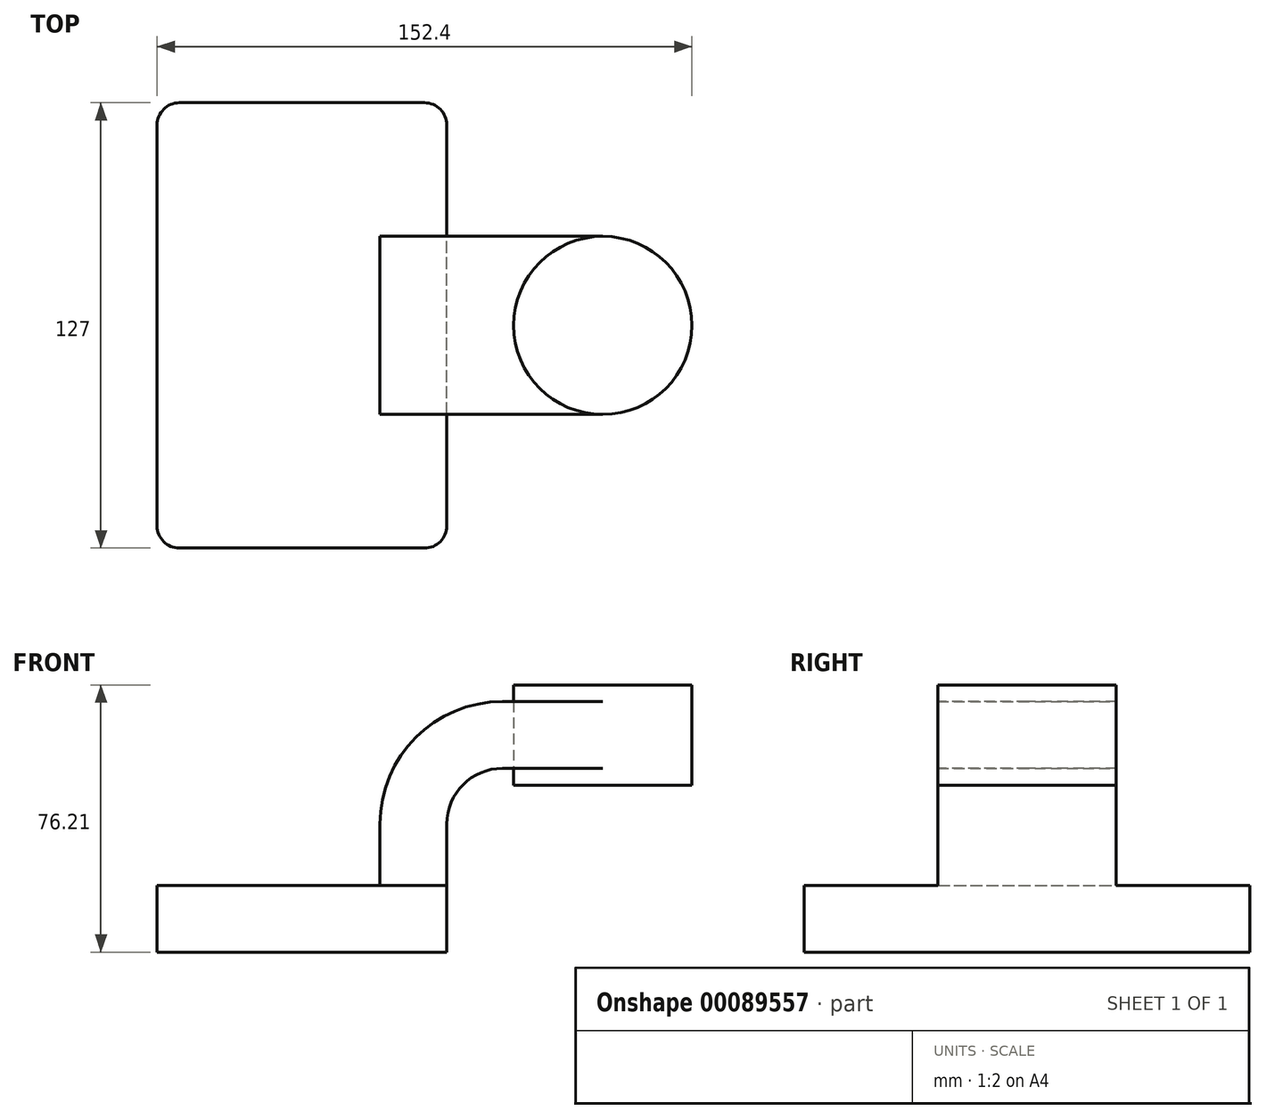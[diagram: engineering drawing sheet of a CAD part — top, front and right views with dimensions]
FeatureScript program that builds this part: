
annotation { "Feature Type Name" : "Feature", "Feature Type Description" : "" }
export const myFeature = defineFeature(function(context is Context, id is Id, definition is map)
    precondition{}
    {
        {
            var Q0;
            Q0=qCreatedBy(makeId("Front.planeOp"),FACE);
            var sketch = newSketch(context, id + "F0", { "sketchPlane" : qUnion([Q0])});
            skLineSegment(sketch, "E0.bottom", {"start": v(-41.28, -9.53) * mm, "end": v(41.28, -9.53) * mm});
            skLineSegment(sketch, "E0.top", {"start": v(-41.28, 9.52) * mm, "end": v(41.28, 9.52) * mm});
            skLineSegment(sketch, "E0.left", {"start": v(-41.28, -9.53) * mm, "end": v(-41.28, 9.53) * mm});
            skLineSegment(sketch, "E0.right", {"start": v(41.28, -9.53) * mm, "end": v(41.28, 9.53) * mm});
            skPoint(sketch, "E0.middle", {"position": v(0, 0) * mm});
            skLineSegment(sketch, "E1.bottom", {"start": v(60.33, 38.1) * mm, "end": v(111.12, 38.1) * mm});
            skLineSegment(sketch, "E1.top", {"start": v(60.32, 66.67) * mm, "end": v(111.12, 66.67) * mm});
            skLineSegment(sketch, "E1.left", {"start": v(60.33, 38.1) * mm, "end": v(60.32, 66.67) * mm});
            skLineSegment(sketch, "E1.right", {"start": v(111.12, 38.1) * mm, "end": v(111.12, 66.67) * mm});
            skPoint(sketch, "E1.middle", {"position": v(85.72, 52.39) * mm});
            skLineSegment(sketch, "E2", {"start": v(41.27, 9.53) * mm, "end": v(41.27, 27) * mm});
            skArc(sketch, "E3", {"start": v(41.27, 27) * mm, "mid": v(45.92, 38.23) * mm, "end": v(57.15, 42.88) * mm});
            skLineSegment(sketch, "E4", {"start": v(57.15, 42.88) * mm, "end": v(85.72, 42.88) * mm});
            skLineSegment(sketch, "E5.0", {"start": v(57.15, 61.93) * mm, "end": v(85.72, 61.93) * mm});
            skArc(sketch, "E5.1", {"start": v(22.22, 27) * mm, "mid": v(32.45, 51.7) * mm, "end": v(57.15, 61.93) * mm});
            skLineSegment(sketch, "E5.2", {"start": v(22.22, 9.53) * mm, "end": v(22.22, 27) * mm});
            skFitSpline(sketch, "E6", {"points": [v(-41.28, 9.52) * mm, v(57.15, 61.93) * mm], "startDerivative": vector(0, 93.07) * mm, "endDerivative": vector(213.39, 0) * mm});
            skLineSegment(sketch, "E7", {"start": v(85.72, 38.1) * mm, "end": v(85.72, 66.67) * mm});
            skSolve(sketch);
        }
        {
            var Q0;
            Q0=makeQuery(id+"F0.imprint","IMPRINT",FACE,{"disambiguationData":[TD([[makeQuery(id+"F0.imprint","IMPRINT",EDGE,{"derivedFrom":sQuery(id+"F0.wireOp",EDGE,"E0.bottom")}),1.0]])]});
            extrude(context, id + "F1", {"entities" : qUnion([Q0]), "endBound" : BoundingType.SYMMETRIC, "depth" : 127 * mm});
        }
        {
            var Q0;
            {var subQ1=sQuery(id+"F0.wireOp",EDGE,"E2");Q0=makeQuery(id+"F0.imprint","IMPRINT",FACE,{"disambiguationData":[TD([[makeQuery(id+"F0.imprint","IMPRINT",EDGE,{"derivedFrom":subQ1}),1.0]])]});}
            var Q1;
            {var subQ5=sQuery(id+"F0.wireOp",EDGE,"NmMJWUsX-LFJ7-nUgh-SmCF-FdiohrqBFDPA");Q1=makeQuery(id+"F0.imprint","IMPRINT",FACE,{"disambiguationData":[TD([[makeQuery(id+"F0.imprint","IMPRINT",EDGE,{"derivedFrom":subQ5}),1.0]])]});}
            var Q2;
            {var subQ0=sQuery(id+"F0.wireOp",EDGE,"E4");var subQ1=sQuery(id+"F0.wireOp",EDGE,"E1.left");var subQ2=makeQuery(id+"F0.imprint","INTERSECT",VERTEX,{"derivedFrom":[subQ1,subQ0]});Q2=makeQuery(id+"F0.imprint","IMPRINT",FACE,{"disambiguationData":[TD([[makeQuery(id+"F0.imprint","IMPRINT",EDGE,{"disambiguationData":[TD([[subQ2,-1.0]])],"derivedFrom":subQ1}),-1.0]])]});}
            extrude(context, id + "F2", {"entities" : qUnion([Q0, Q1, Q2]), "operationType" : NewBodyOperationType.ADD, "endBound" : BoundingType.SYMMETRIC, "depth" : 50.8 * mm});
        }
        {
            var Q0;
            Q0=makeQuery(id+"F0.imprint","IMPRINT",FACE,{"disambiguationData":[TD([[makeQuery(id+"F0.imprint","IMPRINT",EDGE,{"derivedFrom":sQuery(id+"F0.wireOp",EDGE,"E5.1")}),1.0]])]});
            extrude(context, id + "F3", {"entities" : qUnion([Q0]), "operationType" : NewBodyOperationType.ADD, "endBound" : BoundingType.SYMMETRIC, "depth" : 15.88 * mm});
        }
        {
            var Q0;
            {var subQ0=sQuery(id+"F0.wireOp",EDGE,"E1.right");Q0=makeQuery(id+"F0.imprint","IMPRINT",FACE,{"disambiguationData":[TD([[makeQuery(id+"F0.imprint","IMPRINT",EDGE,{"derivedFrom":subQ0}),1.0]])]});}
            var Q1;
            Q1=sQuery(id+"F0.wireOp",EDGE,"E7");
            revolve(context, id + "F4", {"entities" : qUnion([Q0]), "axis" : qUnion([Q1]), "revolveType" : RevolveType.FULL});
        }
        {
            var Q0;
            Q0=makeQuery(id+"F1.opExtrude","CAP_EDGE",EDGE,{"disambiguationData":[OSD([sQuery(id+"F0.wireOp",EDGE,"E0.left")])],"isStart":false});
            var Q1;
            Q1=makeQuery(id+"F1.opExtrude","CAP_EDGE",EDGE,{"disambiguationData":[OSD([sQuery(id+"F0.wireOp",EDGE,"E0.right")])],"isStart":false});
            var Q2;
            Q2=makeQuery(id+"F1.opExtrude","CAP_EDGE",EDGE,{"disambiguationData":[OSD([sQuery(id+"F0.wireOp",EDGE,"E0.right")])],"isStart":true});
            var Q3;
            Q3=makeQuery(id+"F1.opExtrude","CAP_EDGE",EDGE,{"disambiguationData":[OSD([sQuery(id+"F0.wireOp",EDGE,"E0.left")])],"isStart":true});
            fillet(context, id + "F5", {"entities" : qUnion([Q0, Q1, Q2, Q3]), "radius" : 6.35 * mm, "tangentPropagation" : true, "allowEdgeOverflow" : false});
        }
    });
